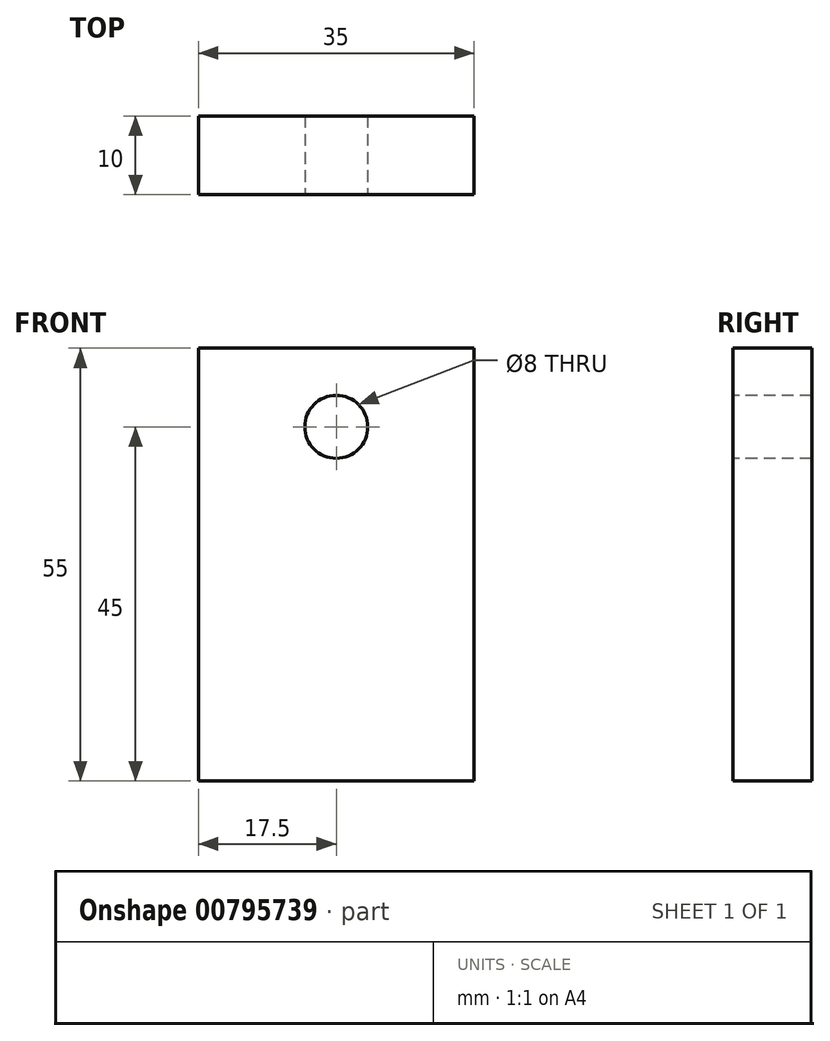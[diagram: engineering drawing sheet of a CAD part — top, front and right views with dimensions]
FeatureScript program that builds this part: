
annotation { "Feature Type Name" : "Feature", "Feature Type Description" : "" }
export const myFeature = defineFeature(function(context is Context, id is Id, definition is map)
    precondition{}
    {
        {
            var Q0;
            Q0=qCreatedBy(makeId("Front.planeOp"),FACE);
            var sketch = newSketch(context, id + "F0", { "sketchPlane" : qUnion([Q0])});
            skLineSegment(sketch, "E0.bottom", {"start": v(17.5, -27.5) * mm, "end": v(-17.5, -27.5) * mm});
            skLineSegment(sketch, "E0.top", {"start": v(17.5, 27.5) * mm, "end": v(-17.5, 27.5) * mm});
            skLineSegment(sketch, "E0.left", {"start": v(17.5, -27.5) * mm, "end": v(17.5, 27.5) * mm});
            skLineSegment(sketch, "E0.right", {"start": v(-17.5, -27.5) * mm, "end": v(-17.5, 27.5) * mm});
            skPoint(sketch, "E0.middle", {"position": v(0, 0) * mm});
            skSolve(sketch);
        }
        {
            var Q0;
            Q0=makeQuery(id+"F0.imprint","IMPRINT",FACE,{"disambiguationData":[TD([[makeQuery(id+"F0.imprint","IMPRINT",EDGE,{"derivedFrom":sQuery(id+"F0.wireOp",EDGE,"E0.bottom")}),-1.0]])]});
            extrude(context, id + "F1", {"entities" : qUnion([Q0]), "depth" : 10 * mm, "offsetDistance" : 25 * mm});
        }
        {
            var Q0;
            Q0=makeQuery(id+"F1.opExtrude","CAP_FACE",FACE,{"disambiguationData":[OSD([sQuery(id+"F0.wireOp",EDGE,"E0.bottom"),sQuery(id+"F0.wireOp",EDGE,"E0.top"),sQuery(id+"F0.wireOp",EDGE,"E0.left"),sQuery(id+"F0.wireOp",EDGE,"E0.right")])],"isStart":false});
            var sketch = newSketch(context, id + "F2", { "sketchPlane" : qUnion([Q0])});
            skLineSegment(sketch, "E1", {"start": v(0, 27.5) * mm, "end": v(0, 17.5) * mm, "construction": true});
            skCircle(sketch, "E2", {"center": v(0, 17.5) * mm, "radius": 4 * mm});
            skSolve(sketch);
        }
        {
            var Q0;
            Q0=makeQuery(id+"F2.imprint","IMPRINT",FACE,{"disambiguationData":[TD([[makeQuery(id+"F2.imprint","IMPRINT",EDGE,{"derivedFrom":sQuery(id+"F2.wireOp",EDGE,"E2")}),1.0]])]});
            extrude(context, id + "F3", {"entities" : qUnion([Q0]), "operationType" : NewBodyOperationType.REMOVE, "endBound" : BoundingType.THROUGH_ALL, "oppositeDirection" : true, "depth" : 25 * mm, "offsetDistance" : 25 * mm});
        }
    });
